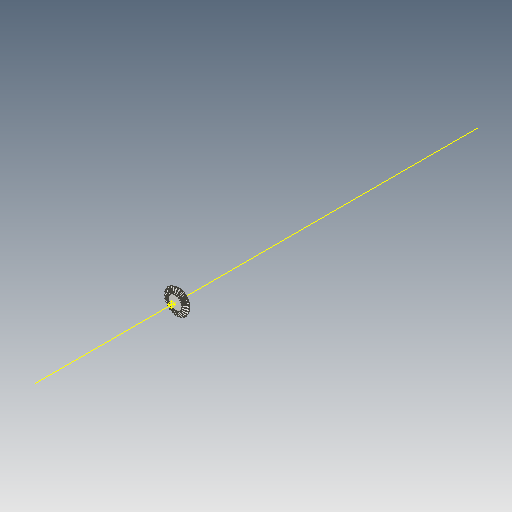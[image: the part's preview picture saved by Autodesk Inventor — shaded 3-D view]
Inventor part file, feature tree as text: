
AUTODESK INVENTOR PART (.ipt)
format: ipt  version: 2021 (Build 250183000, 183)  size: 530,432 bytes
history: native  units: mm
features: other x16, sketch x9, loft x3, pattern_circular x3
ambient origin geometry x6: Origin, XZ Plane, X Axis, Y Axis, Z Axis, Center Point
bodies: Solid1 (feature_tree)
feature tree (31):
  other  "Ponto superior"
  other  "Plano de malha 2"
  other  "Corpo dentado"
  other  "Ponto inicial"
  other  "Plano de dente"
  sketch  "Esboço inicial"  dims[d2=2.699944mm]
  other  "Extremidade"
  loft  "Loft"
  pattern_circular  "Circular Pattern"  [2 undecoded]
  sketch  "Esboço 3D direito"  dims[d3=0.6mm]
  other  "Plano final direito"
  loft  "Transição direita"
  pattern_circular  "Padrão circular direito"  [2 undecoded]
  sketch  "Esboço 3D esquerdo"  dims[d4=0.663381mm]
  other  "Plano final esquerdo"
  loft  "Transição esquerda"
  pattern_circular  "Padrão circular esquerdo"  Count=26 Angle=90.0deg
  other  "Fixar corpo"
  other  "Plano de malha"
  other  "Plano superior"
  sketch  "Esboço de corpo dentado"  dims[d5=90.0deg]
  other  "Plano final"
  sketch  "Esboço final"  dims[d7=0.924244mm]
  other  "Helical Curve Left"
  sketch  "Esboço final esquerdo"  dims[d8=0.939571mm]
  sketch  "Esboço de corpo"  dims[d9=2.2621mm]
  sketch  "Sketch6"  dims[d0=2.6mm d1=2.480067mm]
  other  "Srf1"
  other  "Helical Curve Right"
  sketch  "Esboço final direita"  dims[d11=0.611mm d12=0.547978mm d15=0.557065mm d16=1.341183mm d17=0.0mm d18=90.0deg d19=0.0mm d20=90.0deg d21=260.0mm d22=360.0deg d26=8.972975mm d27=0.30533mm d28=2.6mm d29=-10.47518mm d30=0.547978mm d31=0.557065mm d32=1.341183mm d35=0.0mm d37=0.0mm d39=0.0mm d40=90.0deg d41=260.0mm d42=360.0deg d46=90.0deg d47=90.0deg d48=0.0mm d49=0.0mm d50=90.0deg d51=1.208305mm d52=0.0mm d53=0.0mm d54=0.0mm d56=0.406604mm d57=2.767444mm d58=2.455044mm d59=1.640798mm d60=1.455578mm d61=1.640798mm d62=1.455578mm d65=8.972975mm d66=31.5mm d67=2.6mm d68=-10.47518mm d69=0.30533mm d70=0.557065mm d71=1.341183mm d72=0.547978mm d73=1.455578mm d74=1.640798mm d75=0.0mm d77=0.0mm d79=0.0mm d80=90.0deg d81=260.0mm d82=360.0deg d84=10.0mm d85=20.0mm d86=20.0mm d87=10.0mm d88=0.0mm d89=0.0mm d90=90.0deg d91=90.0deg d92=90.0deg d93=90.0deg]
  other  "Diâmetro do flanco"
note: 4 required parameter values undecoded (feature->parameter linkage not recoverable at this tier; creation-order binding heuristic only, values carry confidence <= 0.55)
